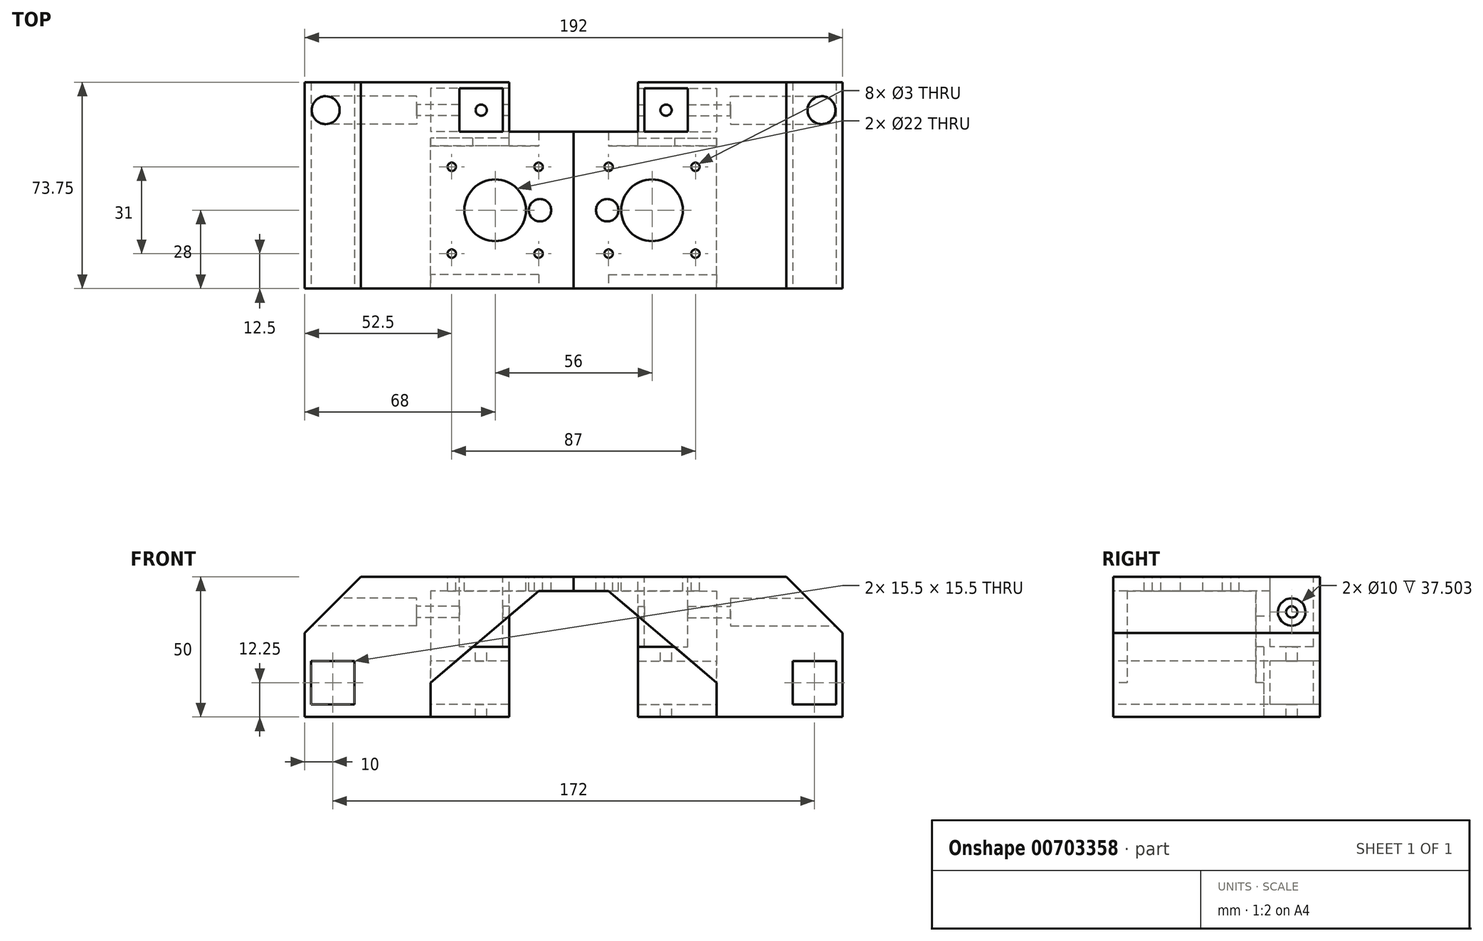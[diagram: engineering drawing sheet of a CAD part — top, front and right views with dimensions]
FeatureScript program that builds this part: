
annotation { "Feature Type Name" : "Feature", "Feature Type Description" : "" }
export const myFeature = defineFeature(function(context is Context, id is Id, definition is map)
    precondition{}
    {
        {
            var Q0;
            Q0=qCreatedBy(makeId("Top.planeOp"),FACE);
            var sketch = newSketch(context, id + "F0", { "sketchPlane" : qUnion([Q0])});
            skLineSegment(sketch, "E0.bottom", {"start": v(-15.5, 15.5) * mm, "end": v(15.5, 15.5) * mm, "construction": true});
            skLineSegment(sketch, "E0.top", {"start": v(-15.5, -15.5) * mm, "end": v(15.5, -15.5) * mm, "construction": true});
            skLineSegment(sketch, "E0.left", {"start": v(-15.5, 15.5) * mm, "end": v(-15.5, -15.5) * mm, "construction": true});
            skLineSegment(sketch, "E0.right", {"start": v(15.5, 15.5) * mm, "end": v(15.5, -15.5) * mm, "construction": true});
            skPoint(sketch, "E0.middle", {"position": v(0, 0) * mm});
            skLineSegment(sketch, "E1.0", {"start": v(28, 28) * mm, "end": v(28, -28) * mm});
            skLineSegment(sketch, "E1.1", {"start": v(-28, 28) * mm, "end": v(28, 28) * mm});
            skLineSegment(sketch, "E1.2", {"start": v(-28, 28) * mm, "end": v(-28, -28) * mm});
            skLineSegment(sketch, "E1.3", {"start": v(-28, -28) * mm, "end": v(28, -28) * mm});
            skCircle(sketch, "E2", {"center": v(-15.5, 15.5) * mm, "radius": 1.5 * mm});
            skCircle(sketch, "E3", {"center": v(-15.5, -15.5) * mm, "radius": 1.5 * mm});
            skCircle(sketch, "E4", {"center": v(15.5, -15.5) * mm, "radius": 1.5 * mm});
            skCircle(sketch, "E5", {"center": v(15.5, 15.5) * mm, "radius": 1.5 * mm});
            skLineSegment(sketch, "E6.bottom", {"start": v(-21, 21.15) * mm, "end": v(21, 21.15) * mm, "construction": true});
            skLineSegment(sketch, "E6.top", {"start": v(-21, -21.15) * mm, "end": v(21, -21.15) * mm, "construction": true});
            skLineSegment(sketch, "E6.left", {"start": v(-21, 21.15) * mm, "end": v(-21, -21.15) * mm, "construction": true});
            skLineSegment(sketch, "E6.right", {"start": v(21, 21.15) * mm, "end": v(21, -21.15) * mm, "construction": true});
            skCircle(sketch, "E7", {"center": v(0, 0) * mm, "radius": 11 * mm});
            skCircle(sketch, "E8", {"center": v(-16, 0) * mm, "radius": 4 * mm});
            skLineSegment(sketch, "E9", {"start": v(-5, 28) * mm, "end": v(-5, 45.75) * mm});
            skLineSegment(sketch, "E10", {"start": v(-5, 45.75) * mm, "end": v(15, 45.75) * mm});
            skLineSegment(sketch, "E11", {"start": v(15, 45.75) * mm, "end": v(15, 28) * mm});
            skLineSegment(sketch, "E12", {"start": v(5, 45.75) * mm, "end": v(5, 28) * mm, "construction": true});
            skLineSegment(sketch, "E13.bottom", {"start": v(-2.75, 43.5) * mm, "end": v(12.75, 43.5) * mm});
            skLineSegment(sketch, "E13.left", {"start": v(-2.75, 43.5) * mm, "end": v(-2.75, 28) * mm});
            skLineSegment(sketch, "E13.right", {"start": v(12.75, 43.5) * mm, "end": v(12.75, 28) * mm});
            skPoint(sketch, "E13.middle", {"position": v(5, 35.75) * mm});
            skLineSegment(sketch, "E14.top", {"start": v(-5, 23) * mm, "end": v(15, 23) * mm});
            skLineSegment(sketch, "E14.left", {"start": v(-5, 28) * mm, "end": v(-5, 23) * mm});
            skLineSegment(sketch, "E14.right", {"start": v(15, 28) * mm, "end": v(15, 23) * mm});
            skLineSegment(sketch, "E15", {"start": v(-2.75, 28) * mm, "end": v(12.75, 28) * mm});
            skLineSegment(sketch, "E16", {"start": v(15, 45.75) * mm, "end": v(28, 45.75) * mm});
            skLineSegment(sketch, "E17", {"start": v(28, 45.75) * mm, "end": v(28, 28) * mm});
            skCircle(sketch, "E18", {"center": v(5, 35.75) * mm, "radius": 2 * mm});
            skSolve(sketch);
        }
        {
            var Q0;
            {var subQ0=sQuery(id+"F0.wireOp",EDGE,"E1.0");Q0=makeQuery(id+"F0.imprint","IMPRINT",FACE,{"disambiguationData":[TD([[makeQuery(id+"F0.imprint","IMPRINT",EDGE,{"derivedFrom":subQ0}),-1.0]])]});}
            var Q1;
            Q1=makeQuery(id+"F0.imprint","IMPRINT",FACE,{"disambiguationData":[TD([[makeQuery(id+"F0.imprint","IMPRINT",EDGE,{"derivedFrom":sQuery(id+"F0.wireOp",EDGE,"E14.top")}),1.0]])]});
            extrude(context, id + "F1", {"entities" : qUnion([Q0, Q1]), "oppositeDirection" : true, "depth" : 5 * mm, "offsetDistance" : 25 * mm});
        }
        {
            var Q0;
            Q0=makeQuery(id+"F1.opExtrude","SWEPT_FACE",FACE,{"disambiguationData":[OSD([sQuery(id+"F0.wireOp",EDGE,"E1.0")])]});
            var sketch = newSketch(context, id + "F2", { "sketchPlane" : qUnion([Q0])});
            skLineSegment(sketch, "E19.bottom", {"start": v(-28, 0) * mm, "end": v(45.75, 0) * mm});
            skLineSegment(sketch, "E19.top", {"start": v(-28, -50) * mm, "end": v(45.75, -50) * mm});
            skLineSegment(sketch, "E19.left", {"start": v(-28, 0) * mm, "end": v(-28, -50) * mm});
            skLineSegment(sketch, "E19.right", {"start": v(45.75, 0) * mm, "end": v(45.75, -50) * mm});
            skLineSegment(sketch, "E20", {"start": v(-28, -25) * mm, "end": v(45.75, -25) * mm});
            skCircle(sketch, "E21", {"center": v(35.75, -12.5) * mm, "radius": 2 * mm});
            skCircle(sketch, "E22", {"center": v(35.75, -12.5) * mm, "radius": 5 * mm});
            skLineSegment(sketch, "E23", {"start": v(25.75, -25) * mm, "end": v(25.75, -50) * mm});
            skLineSegment(sketch, "E24.bottom", {"start": v(43.5, -45.5) * mm, "end": v(28, -45.5) * mm});
            skLineSegment(sketch, "E24.top", {"start": v(43.5, -30) * mm, "end": v(28, -30) * mm});
            skLineSegment(sketch, "E24.left", {"start": v(43.5, -45.5) * mm, "end": v(43.5, -30) * mm});
            skLineSegment(sketch, "E24.right", {"start": v(28, -45.5) * mm, "end": v(28, -30) * mm});
            skSolve(sketch);
        }
        {
            var Q0;
            {var subQ2=sQuery(id+"F2.wireOp",EDGE,"E20");Q0=makeQuery(id+"F2.imprint","IMPRINT",FACE,{"disambiguationData":[TD([[makeQuery(id+"F2.imprint","IMPRINT",EDGE,{"derivedFrom":subQ2}),1.0]])]});}
            var Q1;
            {var subQ0=sQuery(id+"F2.wireOp",EDGE,"E19.bottom");Q1=makeQuery(id+"F2.imprint","IMPRINT",FACE,{"disambiguationData":[TD([[makeQuery(id+"F2.imprint","IMPRINT",EDGE,{"derivedFrom":subQ0}),1.0]])]});}
            var Q2;
            {var subQ0=sQuery(id+"F2.wireOp",EDGE,"E19.top");Q2=makeQuery(id+"F2.imprint","IMPRINT",FACE,{"disambiguationData":[TD([[makeQuery(id+"F2.imprint","IMPRINT",EDGE,{"derivedFrom":subQ0}),1.0]])]});}
            var Q3;
            {var subQ3=sQuery(id+"F2.wireOp",EDGE,"E23");Q3=makeQuery(id+"F2.imprint","IMPRINT",FACE,{"disambiguationData":[TD([[makeQuery(id+"F2.imprint","IMPRINT",EDGE,{"derivedFrom":subQ3}),1.0]])]});}
            var Q4;
            Q4=makeQuery(id+"F2.imprint","IMPRINT",FACE,{"disambiguationData":[TD([[makeQuery(id+"F2.imprint","IMPRINT",EDGE,{"derivedFrom":sQuery(id+"F2.wireOp",EDGE,"E24.bottom")}),-1.0]])]});
            extrude(context, id + "F3", {"entities" : qUnion([Q0, Q1, Q2, Q3, Q4]), "operationType" : NewBodyOperationType.ADD, "oppositeDirection" : true, "depth" : 5 * mm, "offsetDistance" : 25 * mm, "hasSecondDirection" : true, "secondDirectionOppositeDirection" : false, "secondDirectionDepth" : 40 * mm});
        }
        {
            var Q0;
            Q0=makeQuery(id+"F3.boolean.opBoolean","MERGE",FACE,{"derivedFrom":[makeQuery(id+"F1.opExtrude","SWEPT_FACE",FACE,{"disambiguationData":[OSD([sQuery(id+"F0.wireOp",EDGE,"E1.3")])]}),makeQuery(id+"F3.opExtrude","SWEPT_FACE",FACE,{"disambiguationData":[OSD([sQuery(id+"F2.wireOp",EDGE,"E19.left")])]})]});
            var sketch = newSketch(context, id + "F4", { "sketchPlane" : qUnion([Q0])});
            skLineSegment(sketch, "E25", {"start": v(58, -50) * mm, "end": v(58, 0) * mm, "construction": true});
            skLineSegment(sketch, "E26", {"start": v(23, -37.75) * mm, "end": v(68, -37.75) * mm, "construction": true});
            skLineSegment(sketch, "E27", {"start": v(23, -25.25) * mm, "end": v(68, -25.25) * mm, "construction": true});
            skLineSegment(sketch, "E28", {"start": v(23, -37.75) * mm, "end": v(-15.5, -5) * mm});
            skLineSegment(sketch, "E29", {"start": v(68, -20) * mm, "end": v(48, 0) * mm});
            skLineSegment(sketch, "E30.bottom", {"start": v(65.75, -30) * mm, "end": v(50.25, -30) * mm});
            skLineSegment(sketch, "E30.top", {"start": v(65.75, -45.5) * mm, "end": v(50.25, -45.5) * mm});
            skLineSegment(sketch, "E30.left", {"start": v(65.75, -30) * mm, "end": v(65.75, -45.5) * mm});
            skLineSegment(sketch, "E30.right", {"start": v(50.25, -30) * mm, "end": v(50.25, -45.5) * mm});
            skPoint(sketch, "E30.middle", {"position": v(58, -37.75) * mm});
            skSolve(sketch);
        }
        {
            var Q0;
            Q0=makeQuery(id+"F4.imprint","IMPRINT",FACE,{"disambiguationData":[TD([[makeQuery(id+"F4.imprint","IMPRINT",EDGE,{"derivedFrom":sQuery(id+"F4.wireOp",EDGE,"E30.bottom")}),1.0]])]});
            extrude(context, id + "F5", {"entities" : qUnion([Q0]), "operationType" : NewBodyOperationType.REMOVE, "endBound" : BoundingType.THROUGH_ALL, "oppositeDirection" : true, "depth" : 25 * mm, "offsetDistance" : 25 * mm});
        }
        {
            var Q0;
            {var subQ0=sQuery(id+"F4.wireOp",EDGE,"E29");Q0=makeQuery(id+"F4.imprint","IMPRINT",FACE,{"disambiguationData":[TD([[makeQuery(id+"F4.imprint","IMPRINT",EDGE,{"derivedFrom":subQ0}),-1.0]])]});}
            extrude(context, id + "F6", {"entities" : qUnion([Q0]), "operationType" : NewBodyOperationType.REMOVE, "endBound" : BoundingType.THROUGH_ALL, "oppositeDirection" : true, "depth" : 51 * mm, "offsetDistance" : 25 * mm, "hasSecondDirection" : true, "secondDirectionOppositeDirection" : false, "secondDirectionDepth" : 4 * mm});
        }
        {
            var Q0;
            {var subQ0=sQuery(id+"F4.wireOp",EDGE,"E28");Q0=makeQuery(id+"F4.imprint","IMPRINT",FACE,{"disambiguationData":[TD([[makeQuery(id+"F4.imprint","IMPRINT",EDGE,{"derivedFrom":subQ0}),-1.0]])]});}
            extrude(context, id + "F7", {"entities" : qUnion([Q0]), "operationType" : NewBodyOperationType.ADD, "oppositeDirection" : true, "depth" : 56 * mm, "offsetDistance" : 25 * mm, "hasSecondDirection" : true, "secondDirectionOppositeDirection" : true, "secondDirectionDepth" : 51 * mm});
        }
        {
            var Q0;
            {var subQ0=sQuery(id+"F4.wireOp",EDGE,"E28");Q0=makeQuery(id+"F4.imprint","IMPRINT",FACE,{"disambiguationData":[TD([[makeQuery(id+"F4.imprint","IMPRINT",EDGE,{"derivedFrom":subQ0}),-1.0]])]});}
            extrude(context, id + "F8", {"entities" : qUnion([Q0]), "operationType" : NewBodyOperationType.ADD, "oppositeDirection" : true, "depth" : 5 * mm, "offsetDistance" : 25 * mm});
        }
        {
            var Q0;
            {var subQ4=sQuery(id+"F0.wireOp",EDGE,"E9");Q0=makeQuery(id+"F0.imprint","IMPRINT",FACE,{"disambiguationData":[TD([[makeQuery(id+"F0.imprint","IMPRINT",EDGE,{"derivedFrom":subQ4}),-1.0]])]});}
            var Q1;
            Q1=makeQuery(id+"F0.imprint","IMPRINT",FACE,{"disambiguationData":[TD([[makeQuery(id+"F0.imprint","IMPRINT",EDGE,{"derivedFrom":sQuery(id+"F0.wireOp",EDGE,"E14.top")}),1.0]])]});
            var Q2;
            {var subQ2=sQuery(id+"F0.wireOp",EDGE,"E11");Q2=makeQuery(id+"F0.imprint","IMPRINT",FACE,{"disambiguationData":[TD([[makeQuery(id+"F0.imprint","IMPRINT",EDGE,{"derivedFrom":subQ2}),1.0]])]});}
            extrude(context, id + "F9", {"entities" : qUnion([Q0, Q1, Q2]), "operationType" : NewBodyOperationType.ADD, "oppositeDirection" : true, "depth" : 25 * mm, "offsetDistance" : 25 * mm});
        }
        {
            var Q0;
            Q0=makeQuery(id+"F2.imprint","IMPRINT",FACE,{"disambiguationData":[TD([[makeQuery(id+"F2.imprint","IMPRINT",EDGE,{"derivedFrom":sQuery(id+"F2.wireOp",EDGE,"E21")}),1.0]])]});
            extrude(context, id + "F10", {"entities" : qUnion([Q0]), "operationType" : NewBodyOperationType.REMOVE, "oppositeDirection" : true, "depth" : 40 * mm, "offsetDistance" : 25 * mm});
        }
        {
            var Q0;
            {var subQ3=sQuery(id+"F2.wireOp",EDGE,"E23");Q0=makeQuery(id+"F2.imprint","IMPRINT",FACE,{"disambiguationData":[TD([[makeQuery(id+"F2.imprint","IMPRINT",EDGE,{"derivedFrom":subQ3}),1.0]])]});}
            extrude(context, id + "F11", {"entities" : qUnion([Q0]), "operationType" : NewBodyOperationType.ADD, "oppositeDirection" : true, "depth" : 33 * mm, "offsetDistance" : 25 * mm});
        }
        {
            var Q0;
            Q0=makeQuery(id+"F0.imprint","IMPRINT",FACE,{"disambiguationData":[TD([[makeQuery(id+"F0.imprint","IMPRINT",EDGE,{"derivedFrom":sQuery(id+"F0.wireOp",EDGE,"E18")}),1.0]])]});
            extrude(context, id + "F12", {"entities" : qUnion([Q0]), "operationType" : NewBodyOperationType.REMOVE, "endBound" : BoundingType.THROUGH_ALL, "oppositeDirection" : true, "depth" : 25 * mm, "offsetDistance" : 25 * mm});
        }
        {
            var Q0;
            Q0=makeQuery(id+"F1.opExtrude","SWEPT_BODY",BODY,{"disambiguationData":[OSD([sQuery(id+"F0.wireOp",EDGE,"E1.0"),sQuery(id+"F0.wireOp",EDGE,"E1.1"),sQuery(id+"F0.wireOp",EDGE,"E1.2"),sQuery(id+"F0.wireOp",EDGE,"E1.3"),sQuery(id+"F0.wireOp",EDGE,"E2"),sQuery(id+"F0.wireOp",EDGE,"E3"),sQuery(id+"F0.wireOp",EDGE,"E4"),sQuery(id+"F0.wireOp",EDGE,"E5"),sQuery(id+"F0.wireOp",EDGE,"E7"),sQuery(id+"F0.wireOp",EDGE,"E8")])]});
            var Q1;
            Q1=makeQuery(id+"F1.opExtrude","SWEPT_FACE",FACE,{"disambiguationData":[OSD([sQuery(id+"F0.wireOp",EDGE,"E1.2")])]});
            mirror(context, id + "F13", {"entities" : qUnion([Q0]), "mirrorPlane" : qUnion([Q1])});
        }
    });
